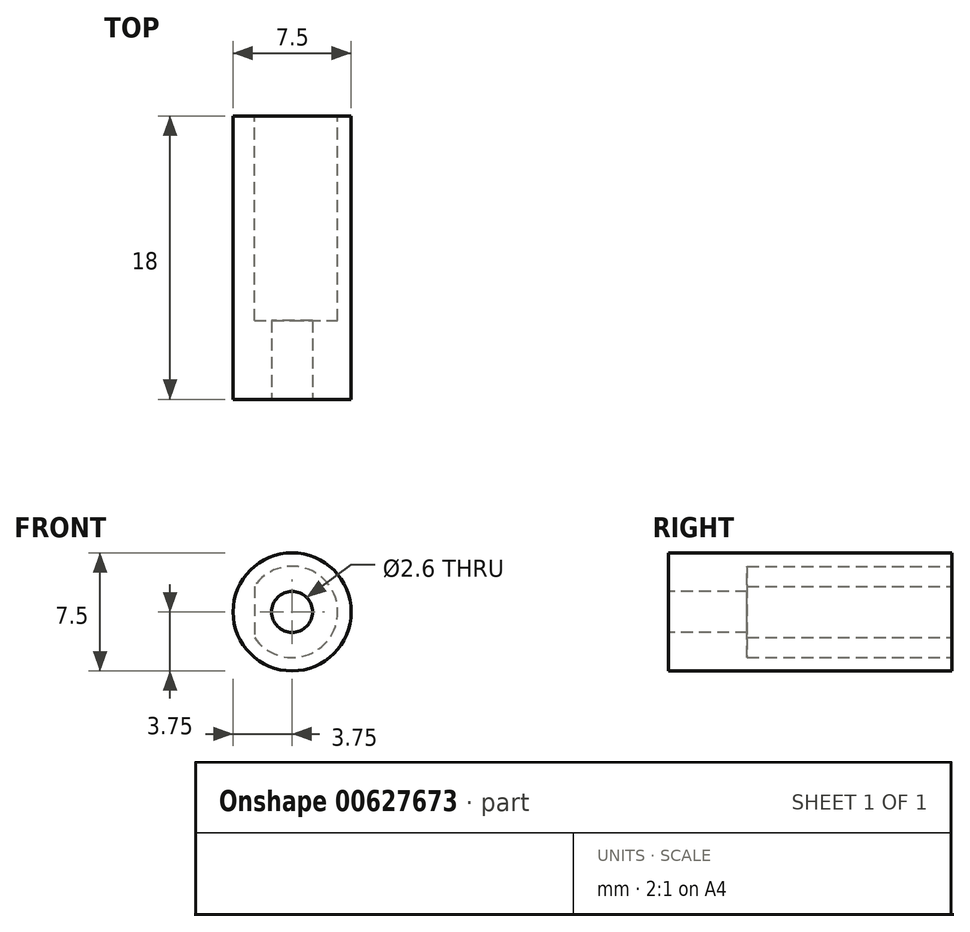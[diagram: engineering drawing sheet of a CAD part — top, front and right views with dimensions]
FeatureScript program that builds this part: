
annotation { "Feature Type Name" : "Feature", "Feature Type Description" : "" }
export const myFeature = defineFeature(function(context is Context, id is Id, definition is map)
    precondition{}
    {
        {
            var Q0;
            Q0=qCreatedBy(makeId("Front.planeOp"),FACE);
            var sketch = newSketch(context, id + "F0", { "sketchPlane" : qUnion([Q0])});
            skCircle(sketch, "E0", {"center": v(0, 0) * mm, "radius": 3 * mm, "construction": true});
            skCircle(sketch, "E1", {"center": v(0, 0) * mm, "radius": 3.75 * mm});
            skSolve(sketch);
        }
        {
            var Q0;
            Q0=makeQuery(id+"F0.imprint","IMPRINT",FACE,{"disambiguationData":[TD([[makeQuery(id+"F0.imprint","IMPRINT",EDGE,{"derivedFrom":sQuery(id+"F0.wireOp",EDGE,"E1")}),1.0]])]});
            var Q1;
            Q1=sQuery(id+"F0.wireOp",EDGE,"E1");
            extrude(context, id + "F1", {"entities" : qUnion([Q0]), "surfaceEntities" : qUnion([Q1]), "depth" : 18 * mm, "offsetDistance" : 25 * mm});
        }
        {
            var Q0;
            Q0=makeQuery(id+"F1.opExtrude","CAP_FACE",FACE,{"disambiguationData":[OSD([sQuery(id+"F0.wireOp",EDGE,"E1")])],"isStart":true});
            var sketch = newSketch(context, id + "F2", { "sketchPlane" : qUnion([Q0])});
            skArc(sketch, "E2", {"start": v(2, 1.5) * mm, "mid": v(-2.5, 0) * mm, "end": v(2, -1.5) * mm, "construction": true});
            skLineSegment(sketch, "E3", {"start": v(2, 1.5) * mm, "end": v(2, -1.5) * mm, "construction": true});
            skArc(sketch, "E4.0", {"start": v(2.4, 1.63) * mm, "mid": v(-2.9, 0) * mm, "end": v(2.4, -1.63) * mm});
            skLineSegment(sketch, "E4.1", {"start": v(2.4, 1.63) * mm, "end": v(2.4, -1.63) * mm});
            skSolve(sketch);
        }
        {
            var Q0;
            Q0=makeQuery(id+"F2.imprint","IMPRINT",FACE,{"disambiguationData":[TD([[makeQuery(id+"F2.imprint","IMPRINT",EDGE,{"derivedFrom":sQuery(id+"F2.wireOp",EDGE,"E4.0")}),1.0]])]});
            var Q1;
            Q1=makeQuery(id+"F1.opExtrude","CAP_FACE",FACE,{"disambiguationData":[OSD([sQuery(id+"F0.wireOp",EDGE,"E1")])],"isStart":false});
            extrude(context, id + "F3", {"entities" : qUnion([Q0]), "operationType" : NewBodyOperationType.REMOVE, "endBound" : BoundingType.UP_TO_SURFACE, "oppositeDirection" : true, "depth" : 25 * mm, "endBoundEntityFace" : qUnion([Q1]), "hasOffset" : true, "offsetDistance" : 5 * mm});
        }
        {
            var Q0;
            Q0=makeQuery(id+"F1.opExtrude","CAP_FACE",FACE,{"disambiguationData":[OSD([sQuery(id+"F0.wireOp",EDGE,"E1")])],"isStart":false});
            var sketch = newSketch(context, id + "F4", { "sketchPlane" : qUnion([Q0])});
            skCircle(sketch, "E5", {"center": v(0, 0) * mm, "radius": 1.3 * mm});
            skSolve(sketch);
        }
        {
            var Q0;
            Q0 = qSketchRegion(id + "F4", true);
            extrude(context, id + "F5", {"entities" : qUnion([Q0]), "operationType" : NewBodyOperationType.REMOVE, "endBound" : BoundingType.THROUGH_ALL, "oppositeDirection" : true, "depth" : 25 * mm, "offsetDistance" : 25 * mm});
        }
    });
